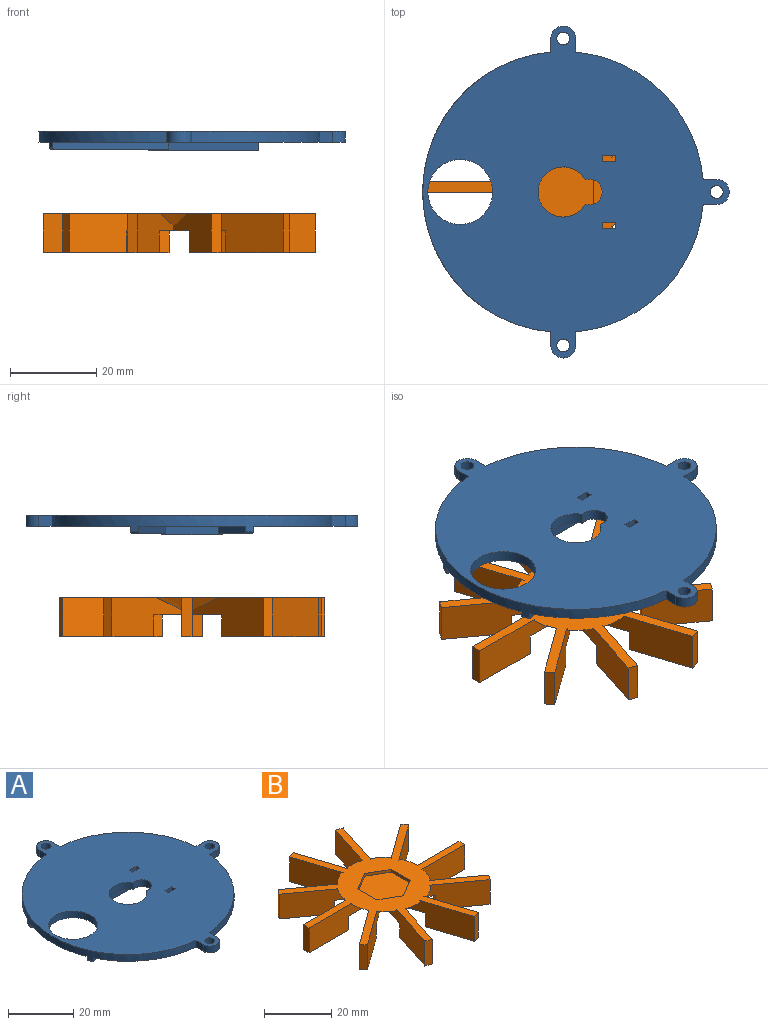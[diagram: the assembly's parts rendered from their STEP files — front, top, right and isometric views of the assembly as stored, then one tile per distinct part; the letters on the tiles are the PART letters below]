
ASSEMBLY  parts=2 mates=1
PART A: 47 faces, bbox 70.9x76.8x4.5 mm
  f0: plane 25.5x24.61mm, normal (0,0,-1), area 288.6mm2, adj f2,f6,f31,f40,f42
  f1: plane 76.8x67.66mm, normal (0,0,-1), area 2460.6mm2, adj f6,f7,f8,f9,f10,f11,f12,f13
  f2: plane 14x2mm, normal (-1,0,0), area 25.2mm2, adj f0,f18,f21,f38,f40,f41,f42,f44
  f3: plane 5.8x5.8mm, normal (0,0,-1), area 7.2mm2, adj f17,f33,f34
  f4: plane 5.8x5.8mm, normal (0,0,-1), area 7.2mm2, adj f17,f33,f36
  f5: plane 17.2x11.6mm, normal (0,0,-1), area 129.8mm2, adj f17,f28,f34,f35,f36
  f6: cylinder r=32.5mm len=64.74mm, axis (0,0,-1), area 245.6mm2, adj f0,f1,f7,f27,f32,f39,f40,f42
  f7: plane 3.13x2.5mm, normal (-1,0,0), area 7.8mm2, adj f1,f6,f8,f32
  f8: cylinder r=2.9mm len=5.8mm, axis (0,0,-1), area 22.8mm2, adj f1,f7,f9,f32
  f9: plane 3.13x2.5mm, normal (1,0,0), area 7.8mm2, adj f1,f8,f10,f32
  f10: cylinder r=32.5mm len=29.47mm, axis (0,0,-1), area 113.1mm2, adj f1,f9,f11,f32
  f11: plane 3.13x2.5mm, normal (0,-1,0), area 7.8mm2, adj f1,f10,f12,f32
  f12: cylinder r=2.9mm len=5.8mm, axis (0,0,-1), area 22.8mm2, adj f1,f11,f13,f32
  f13: plane 3.13x2.5mm, normal (0,1,0), area 7.8mm2, adj f1,f12,f14,f32
  f14: cylinder r=32.5mm len=29.47mm, axis (0,0,-1), area 113.1mm2, adj f1,f13,f15,f32
  f15: plane 3.13x2.5mm, normal (1,0,0), area 7.8mm2, adj f1,f14,f16,f32
  f16: cylinder r=2.9mm len=5.8mm, axis (0,0,-1), area 22.8mm2, adj f1,f15,f27,f32
  f17: cylinder r=5.8mm len=11.6mm, axis (0,0,-1), area 76.2mm2, adj f3,f4,f5,f28,f32
  f18: plane 25.4x4.5mm, normal (0,-1,0), area 51.2mm2, adj f1,f2,f19,f29,f32,f37,f38,f43
  f19: plane 2.5x1.5mm, normal (-1,0,0), area 3.8mm2, adj f1,f18,f20,f32
  f20: plane 3x2.5mm, normal (0,1,0), area 7.5mm2, adj f1,f19,f29,f32
  f21: plane 25.4x4.5mm, normal (0,1,0), area 51.2mm2, adj f1,f2,f22,f30,f32,f37,f38,f39
  f22: plane 2.5x1.5mm, normal (1,0,0), area 3.8mm2, adj f1,f21,f23,f32
  f23: plane 3x2.5mm, normal (0,-1,0), area 7.5mm2, adj f1,f22,f30,f32
  f24: cylinder r=1.5mm len=3mm, axis (0,0,-1), area 23.6mm2, adj f1,f32
  f25: cylinder r=1.5mm len=3mm, axis (0,0,-1), area 23.6mm2, adj f1,f32
  f26: cylinder r=1.5mm len=3mm, axis (0,0,-1), area 23.6mm2, adj f1,f32
  f27: plane 3.13x2.5mm, normal (-1,0,0), area 7.8mm2, adj f1,f6,f16,f32
  f28: cylinder r=3mm len=6mm, axis (0,0,-1), area 28.4mm2, adj f5,f17,f32
  f29: plane 2.5x1.5mm, normal (1,0,0), area 3.8mm2, adj f1,f18,f20,f32
  f30: plane 2.5x1.5mm, normal (-1,0,0), area 3.8mm2, adj f1,f21,f23,f32
  f31: cylinder r=7.5mm len=15mm, axis (0,0,-1), area 117.8mm2, adj f0,f32
  f32: plane 76.8x70.9mm, normal (0,0,1), area 3081.4mm2, adj f6,f7,f8,f9,f10,f11,f12,f13
  f33: plane 11.6x2mm, normal (1,0,0), area 23.2mm2, adj f3,f4,f34,f36,f38
  f34: plane 23x2mm, normal (0,-1,0), area 46mm2, adj f3,f5,f33,f35,f38
  f35: plane 11.6x2mm, normal (-1,0,0), area 23.2mm2, adj f5,f34,f36,f38
  f36: plane 23x2mm, normal (0,1,0), area 46mm2, adj f4,f5,f33,f35,f38
  f37: plane 14x2mm, normal (1,0,0), area 28mm2, adj f1,f18,f21,f38
  f38: plane 25.4x14mm, normal (0,0,-1), area 88.8mm2, adj f2,f18,f21,f33,f34,f35,f36,f37
  f39: plane 26.7x7.16mm, normal (0.26,0.97,0), area 44.2mm2, adj f1,f6,f21,f41,f45
  f40: plane 23.08x6.18mm, normal (-0.26,-0.97,0), area 38.2mm2, adj f0,f2,f6,f41,f45
  f41: plane 27.14x7.93mm, normal (0,0,-1), area 48.8mm2, adj f2,f21,f39,f40,f45
  f42: plane 23.08x6.18mm, normal (-0.26,0.97,0), area 38.2mm2, adj f0,f2,f6,f44,f46
  f43: plane 26.7x7.16mm, normal (0.26,-0.97,0), area 44.2mm2, adj f1,f6,f18,f44,f46
  f44: plane 27.14x7.93mm, normal (0,0,-1), area 48.8mm2, adj f2,f18,f42,f43,f46
  f45: torus R=32.1mm, axis (0,0,1), area 1.3mm2, adj f6,f39,f40,f41
  f46: torus R=32.1mm, axis (0,0,1), area 1.3mm2, adj f6,f42,f43,f44
PART B: 90 faces, bbox 63.1x61.5x9.1 mm
  f0: plane 63x61.4mm, normal (0,0,1), area 867.7mm2, adj f6,f7,f8,f11,f13,f18,f19,f20
  f1: plane 0.35x0.22mm, normal (0.95,0.31,0), area 0.1mm2, adj f2,f3,f10,f12
  f2: plane 0.83x0.49mm, normal (-0.31,0.95,0), area 0.2mm2, adj f1,f3,f9,f10
  f3: plane 30.02x30mm, normal (0,0,-1), area 316.7mm2, adj f1,f2,f4,f7,f8,f9,f12,f13
  f4: plane 5x2.28mm, normal (-0.31,0.95,0), area 12mm2, adj f3,f5,f7,f8
  f5: plane 16.43x7.38mm, normal (0,0,-1), area 39.6mm2, adj f4,f6,f7,f8
  f6: plane 9x2.28mm, normal (0.31,-0.95,0), area 21.6mm2, adj f0,f5,f7,f8
  f7: plane 26.82x9mm, normal (-0.95,-0.31,0), area 180.1mm2, adj f0,f3,f4,f5,f6,f22,f73
  f8: plane 26.08x9mm, normal (0.95,0.31,0), area 178.1mm2, adj f0,f3,f4,f5,f6,f11,f13
  f9: plane 0.35x0.22mm, normal (0.95,-0.31,0), area 0.1mm2, adj f2,f3,f10,f68
  f10: cone r=14mm half-angle=74.1deg, axis (0,0,1), area 4.1mm2, adj f1,f2,f9,f12,f14,f15,f21,f24
  f11: cone r=14mm half-angle=74.1deg, axis (0,0,1), area 33.4mm2, adj f0,f8,f13
  f12: plane 0.72x0.56mm, normal (-0.81,0.59,0), area 0.2mm2, adj f1,f3,f10,f21
  f13: plane 22.81x16.57mm, normal (-0.59,-0.81,0), area 180.1mm2, adj f0,f3,f8,f11,f79,f80,f81
  f14: plane 0.35x0.24mm, normal (0,1,0), area 0.1mm2, adj f3,f10,f15,f24
  f15: plane 0.86x0.49mm, normal (-1,0,0), area 0.2mm2, adj f3,f10,f14,f21
  f16: plane 5x2.4mm, normal (-1,0,0), area 12mm2, adj f3,f17,f19,f20
  f17: plane 16.5x2.4mm, normal (0,0,-1), area 39.6mm2, adj f16,f18,f19,f20
  f18: plane 9x2.4mm, normal (1,0,0), area 21.6mm2, adj f0,f17,f19,f20
  f19: plane 28.2x9mm, normal (0,-1,0), area 180.1mm2, adj f0,f3,f16,f17,f18,f34,f82
  f20: plane 27.42x9mm, normal (0,1,0), area 178.1mm2, adj f0,f3,f16,f17,f18,f23,f25
  f21: plane 0.35x0.19mm, normal (0.59,0.81,0), area 0.1mm2, adj f3,f10,f12,f15
  f22: cone r=14mm half-angle=74.1deg, axis (0,0,1), area 33.4mm2, adj f0,f7,f73
  f23: cone r=14mm half-angle=74.1deg, axis (0,0,1), area 33.4mm2, adj f0,f20,f25
  f24: plane 0.73x0.56mm, normal (-0.81,-0.59,0), area 0.2mm2, adj f3,f10,f14,f60
  f25: plane 22.81x16.57mm, normal (0.59,-0.81,0), area 180.1mm2, adj f0,f3,f20,f23,f62,f63,f64
  f26: plane 0.86x0.49mm, normal (1,0,0), area 0.2mm2, adj f3,f10,f28,f33
  f27: plane 28.2x9mm, normal (0,1,0), area 180.1mm2, adj f0,f3,f29,f30,f31,f43,f45
  f28: plane 0.35x0.24mm, normal (0,-1,0), area 0.1mm2, adj f3,f10,f26,f36
  f29: plane 5x2.4mm, normal (1,0,0), area 12mm2, adj f3,f27,f30,f32
  f30: plane 16.5x2.4mm, normal (0,0,-1), area 39.6mm2, adj f27,f29,f31,f32
  f31: plane 9x2.4mm, normal (-1,0,0), area 21.6mm2, adj f0,f27,f30,f32
  f32: plane 27.42x9mm, normal (0,-1,0), area 178.1mm2, adj f0,f3,f29,f30,f31,f35,f37
  f33: plane 0.35x0.19mm, normal (-0.59,-0.81,0), area 0.1mm2, adj f3,f10,f26,f38
  f34: cone r=14mm half-angle=74.1deg, axis (0,0,1), area 33.4mm2, adj f0,f19,f82
  f35: cone r=14mm half-angle=74.1deg, axis (0,0,1), area 33.4mm2, adj f0,f32,f37
  f36: plane 0.72x0.56mm, normal (0.81,0.59,0), area 0.2mm2, adj f3,f10,f28,f74
  f37: plane 22.81x16.57mm, normal (-0.59,0.81,0), area 180.1mm2, adj f0,f3,f32,f35,f75,f76,f77
  f38: plane 0.73x0.56mm, normal (0.81,-0.59,0), area 0.2mm2, adj f3,f10,f33,f44
  f39: plane 22.81x16.57mm, normal (0.59,0.81,0), area 180.1mm2, adj f0,f3,f40,f41,f42,f51,f53
  f40: plane 5x1.94mm, normal (0.81,-0.59,0), area 12mm2, adj f3,f39,f41,f43
  f41: plane 14.76x11.64mm, normal (0,0,-1), area 39.6mm2, adj f39,f40,f42,f43
  f42: plane 9x1.94mm, normal (-0.81,0.59,0), area 21.6mm2, adj f0,f39,f41,f43
  f43: plane 22.18x16.12mm, normal (-0.59,-0.81,0), area 178.1mm2, adj f0,f3,f27,f40,f41,f42,f45
  f44: plane 0.35x0.22mm, normal (-0.95,-0.31,0), area 0.1mm2, adj f3,f10,f38,f46
  f45: cone r=14mm half-angle=74.1deg, axis (0,0,1), area 33.4mm2, adj f0,f27,f43
  f46: plane 0.83x0.49mm, normal (0.31,-0.95,0), area 0.2mm2, adj f3,f10,f44,f52
  f47: plane 26.82x9mm, normal (0.95,0.31,0), area 180.1mm2, adj f0,f3,f48,f49,f50,f59,f61
  f48: plane 5x2.28mm, normal (0.31,-0.95,0), area 12mm2, adj f3,f47,f49,f51
  f49: plane 16.43x7.38mm, normal (0,0,-1), area 39.6mm2, adj f47,f48,f50,f51
  f50: plane 9x2.28mm, normal (-0.31,0.95,0), area 21.6mm2, adj f0,f47,f49,f51
  f51: plane 26.08x9mm, normal (-0.95,-0.31,0), area 178.1mm2, adj f0,f3,f39,f48,f49,f50,f53
  f52: plane 0.35x0.22mm, normal (-0.95,0.31,0), area 0.1mm2, adj f3,f10,f46,f54
  f53: cone r=14mm half-angle=74.1deg, axis (0,0,1), area 33.4mm2, adj f0,f39,f51
  f54: plane 0.83x0.49mm, normal (-0.31,-0.95,0), area 0.2mm2, adj f3,f10,f52,f60
  f55: plane 26.82x9mm, normal (0.95,-0.31,0), area 180.1mm2, adj f0,f3,f56,f57,f58,f65,f66
  f56: plane 5x2.28mm, normal (-0.31,-0.95,0), area 12mm2, adj f3,f55,f57,f59
  f57: plane 16.43x7.38mm, normal (0,0,-1), area 39.6mm2, adj f55,f56,f58,f59
  f58: plane 9x2.28mm, normal (0.31,0.95,0), area 21.6mm2, adj f0,f55,f57,f59
  f59: plane 26.08x9mm, normal (-0.95,0.31,0), area 178.1mm2, adj f0,f3,f47,f56,f57,f58,f61
  f60: plane 0.35x0.19mm, normal (-0.59,0.81,0), area 0.1mm2, adj f3,f10,f24,f54
  f61: cone r=14mm half-angle=74.1deg, axis (0,0,1), area 33.4mm2, adj f0,f47,f59
  f62: plane 5x1.94mm, normal (-0.81,-0.59,0), area 12mm2, adj f3,f25,f63,f65
  f63: plane 14.76x11.64mm, normal (0,0,-1), area 39.6mm2, adj f25,f62,f64,f65
  f64: plane 9x1.94mm, normal (0.81,0.59,0), area 21.6mm2, adj f0,f25,f63,f65
  f65: plane 22.18x16.12mm, normal (-0.59,0.81,0), area 178.1mm2, adj f0,f3,f55,f62,f63,f64,f66
  f66: cone r=14mm half-angle=74.1deg, axis (0,0,1), area 33.4mm2, adj f0,f55,f65
  f67: cone r=14mm half-angle=74.1deg, axis (0,0,1), area 33.4mm2, adj f0,f69,f78
  f68: plane 0.83x0.49mm, normal (0.31,0.95,0), area 0.2mm2, adj f3,f9,f10,f74
  f69: plane 26.82x9mm, normal (-0.95,0.31,0), area 180.1mm2, adj f0,f3,f67,f70,f71,f72,f78
  f70: plane 5x2.28mm, normal (0.31,0.95,0), area 12mm2, adj f3,f69,f71,f73
  f71: plane 16.43x7.38mm, normal (0,0,-1), area 39.6mm2, adj f69,f70,f72,f73
  f72: plane 9x2.28mm, normal (-0.31,-0.95,0), area 21.6mm2, adj f0,f69,f71,f73
  f73: plane 26.08x9mm, normal (0.95,-0.31,0), area 178.1mm2, adj f0,f3,f7,f22,f70,f71,f72
  f74: plane 0.35x0.19mm, normal (0.59,-0.81,0), area 0.1mm2, adj f3,f10,f36,f68
  f75: plane 5x1.94mm, normal (0.81,0.59,0), area 12mm2, adj f3,f37,f76,f78
  f76: plane 14.76x11.64mm, normal (0,0,-1), area 39.6mm2, adj f37,f75,f77,f78
  f77: plane 9x1.94mm, normal (-0.81,-0.59,0), area 21.6mm2, adj f0,f37,f76,f78
  f78: plane 22.18x16.12mm, normal (0.59,-0.81,0), area 178.1mm2, adj f0,f3,f67,f69,f75,f76,f77
  f79: plane 5x1.94mm, normal (-0.81,0.59,0), area 12mm2, adj f3,f13,f80,f82
  f80: plane 14.76x11.64mm, normal (0,0,-1), area 39.6mm2, adj f13,f79,f81,f82
  f81: plane 9x1.94mm, normal (0.81,-0.59,0), area 21.6mm2, adj f0,f13,f80,f82
  f82: plane 22.18x16.12mm, normal (0.59,0.81,0), area 178.1mm2, adj f0,f3,f19,f34,f79,f80,f81
  f83: plane 8.08x1mm, normal (-1,0,0), area 8.1mm2, adj f0,f84,f88,f89
  f84: plane 7x4.04mm, normal (-0.5,-0.87,0), area 8.1mm2, adj f0,f83,f85,f89
  f85: plane 7x4.04mm, normal (0.5,-0.87,0), area 8.1mm2, adj f0,f84,f86,f89
  f86: plane 8.08x1mm, normal (1,0,0), area 8.1mm2, adj f0,f85,f87,f89
  f87: plane 7x4.04mm, normal (0.5,0.87,0), area 8.1mm2, adj f0,f86,f88,f89
  f88: plane 7x4.04mm, normal (-0.5,0.87,0), area 8.1mm2, adj f0,f83,f87,f89
  f89: plane 16.17x14mm, normal (0,0,1), area 169.7mm2, adj f83,f84,f85,f86,f87,f88
PLACE A t=(-16.62,-10.5,32.75)mm fixed
PLACE B t=(-16.62,-10.5,3.25)mm
MATE revolute A.f17 <-> B.f10  axis (0,0,1) through (-16.62,-10.5,35.25)mm
